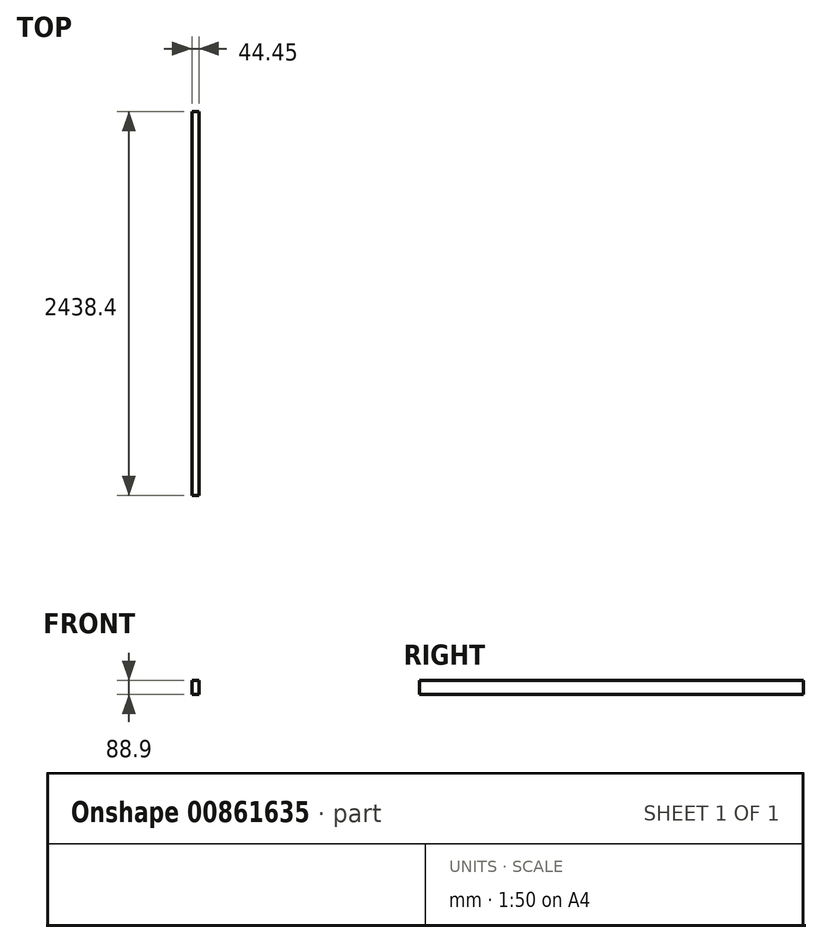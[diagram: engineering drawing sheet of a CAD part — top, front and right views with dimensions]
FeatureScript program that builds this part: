
annotation { "Feature Type Name" : "Feature", "Feature Type Description" : "" }
export const myFeature = defineFeature(function(context is Context, id is Id, definition is map)
    precondition{}
    {
        {
            var Q0;
            Q0=qCreatedBy(makeId("Front.planeOp"),FACE);
            var sketch = newSketch(context, id + "F0", { "sketchPlane" : qUnion([Q0])});
            skLineSegment(sketch, "E0.bottom", {"start": v(0, 0) * mm, "end": v(44.45, 0) * mm});
            skLineSegment(sketch, "E0.top", {"start": v(0, 88.9) * mm, "end": v(44.45, 88.9) * mm});
            skLineSegment(sketch, "E0.left", {"start": v(0, 0) * mm, "end": v(0, 88.9) * mm});
            skLineSegment(sketch, "E0.right", {"start": v(44.45, 0) * mm, "end": v(44.45, 88.9) * mm});
            skSolve(sketch);
        }
        {
            var Q0;
            Q0=makeQuery(id+"F0.imprint","IMPRINT",FACE,{"disambiguationData":[TD([[makeQuery(id+"F0.imprint","IMPRINT",EDGE,{"derivedFrom":sQuery(id+"F0.wireOp",EDGE,"E0.bottom")}),1.0]])]});
            extrude(context, id + "F1", {"entities" : qUnion([Q0]), "depth" : 2438.4 * mm, "offsetDistance" : 25.4 * mm});
        }
    });
